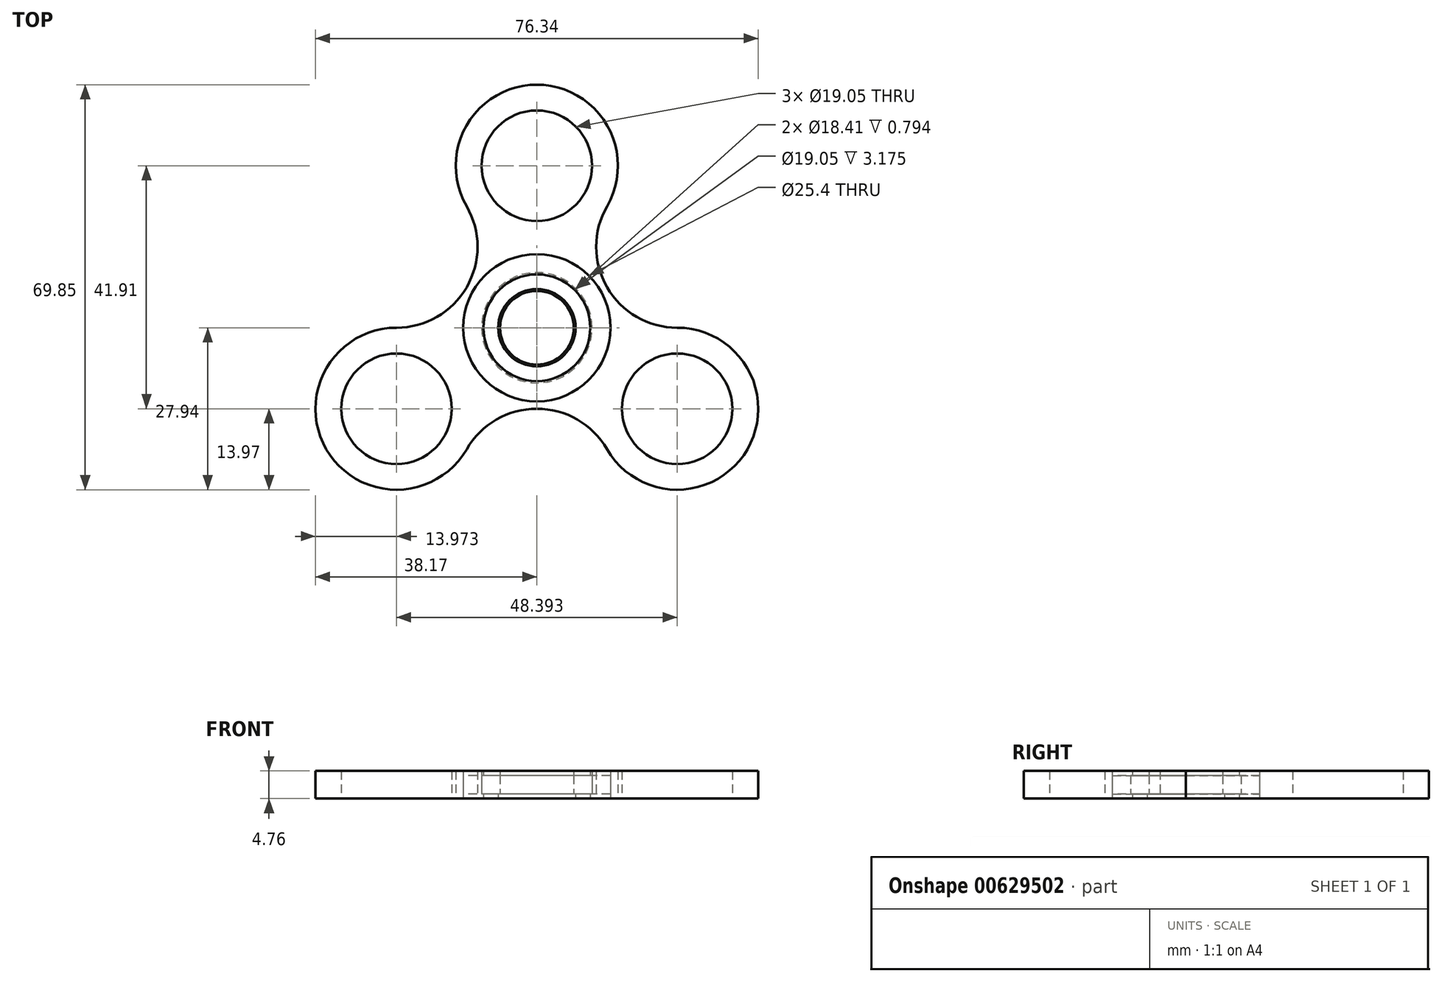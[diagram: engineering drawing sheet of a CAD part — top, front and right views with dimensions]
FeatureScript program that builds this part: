
annotation { "Feature Type Name" : "Feature", "Feature Type Description" : "" }
export const myFeature = defineFeature(function(context is Context, id is Id, definition is map)
    precondition{}
    {
        {
            var Q0;
            Q0=qCreatedBy(makeId("Top.planeOp"),FACE);
            var sketch = newSketch(context, id + "F0", { "sketchPlane" : qUnion([Q0])});
            skCircle(sketch, "E0", {"center": v(0, 0) * mm, "radius": 12.7 * mm});
            skCircle(sketch, "E1", {"center": v(0, 0) * mm, "radius": 9.2 * mm});
            skCircle(sketch, "E2", {"center": v(0, 0) * mm, "radius": 6.67 * mm});
            skSolve(sketch);
        }
        {
            var Q0;
            Q0=makeQuery(id+"F0.imprint","IMPRINT",FACE,{"disambiguationData":[TD([[makeQuery(id+"F0.imprint","IMPRINT",EDGE,{"derivedFrom":sQuery(id+"F0.wireOp",EDGE,"E0")}),1.0]])]});
            var Q1;
            Q1=makeQuery(id+"F0.imprint","IMPRINT",FACE,{"disambiguationData":[TD([[makeQuery(id+"F0.imprint","IMPRINT",EDGE,{"derivedFrom":sQuery(id+"F0.wireOp",EDGE,"E2")}),1.0]])]});
            extrude(context, id + "F1", {"entities" : qUnion([Q0, Q1]), "depth" : 0.8 * mm, "offsetDistance" : 25.4 * mm});
        }
        {
            var Q0;
            Q0=makeQuery(id+"F1.opExtrude","CAP_FACE",FACE,{"disambiguationData":[OSD([sQuery(id+"F0.wireOp",EDGE,"E2")])],"isStart":false});
            var sketch = newSketch(context, id + "F2", { "sketchPlane" : qUnion([Q0])});
            skCircle(sketch, "E3", {"center": v(0, 0) * mm, "radius": 12.7 * mm});
            skCircle(sketch, "E4", {"center": v(0, 0) * mm, "radius": 9.53 * mm});
            skCircle(sketch, "E5", {"center": v(0, 0) * mm, "radius": 6.35 * mm});
            skSolve(sketch);
        }
        {
            var Q0;
            Q0=makeQuery(id+"F2.imprint","IMPRINT",FACE,{"disambiguationData":[TD([[makeQuery(id+"F2.imprint","IMPRINT",EDGE,{"derivedFrom":sQuery(id+"F2.wireOp",EDGE,"E5")}),1.0]])]});
            var Q1;
            Q1=makeQuery(id+"F2.imprint","IMPRINT",FACE,{"disambiguationData":[TD([[makeQuery(id+"F2.imprint","IMPRINT",EDGE,{"derivedFrom":sQuery(id+"F2.wireOp",EDGE,"E3")}),1.0]])]});
            extrude(context, id + "F3", {"entities" : qUnion([Q0, Q1]), "depth" : 3.17 * mm, "offsetDistance" : 25.4 * mm});
        }
        {
            var Q0;
            Q0=makeQuery(id+"F3.opExtrude","CAP_FACE",FACE,{"disambiguationData":[OSD([sQuery(id+"F2.wireOp",EDGE,"E5")])],"isStart":false});
            var sketch = newSketch(context, id + "F4", { "sketchPlane" : qUnion([Q0])});
            skCircle(sketch, "E6", {"center": v(0, 0) * mm, "radius": 12.7 * mm});
            skCircle(sketch, "E7", {"center": v(0, 0) * mm, "radius": 9.2 * mm});
            skCircle(sketch, "E8", {"center": v(0, 0) * mm, "radius": 6.67 * mm});
            skSolve(sketch);
        }
        {
            var Q0;
            Q0=makeQuery(id+"F4.imprint","IMPRINT",FACE,{"disambiguationData":[TD([[makeQuery(id+"F4.imprint","IMPRINT",EDGE,{"derivedFrom":makeQuery(id+"F3.opExtrude","CAP_EDGE",EDGE,{"disambiguationData":[OSD([sQuery(id+"F2.wireOp",EDGE,"E5")])],"isStart":false})}),1.0]])]});
            var Q1;
            Q1=makeQuery(id+"F4.imprint","IMPRINT",FACE,{"disambiguationData":[TD([[makeQuery(id+"F4.imprint","IMPRINT",EDGE,{"derivedFrom":sQuery(id+"F4.wireOp",EDGE,"E6")}),1.0]])]});
            extrude(context, id + "F5", {"entities" : qUnion([Q0, Q1]), "depth" : 0.8 * mm, "offsetDistance" : 25.4 * mm});
        }
        {
            var Q0;
            Q0=qCreatedBy(makeId("Top.planeOp"),FACE);
            var sketch = newSketch(context, id + "F6", { "sketchPlane" : qUnion([Q0])});
            skCircle(sketch, "E9", {"center": v(0, 0) * mm, "radius": 12.7 * mm});
            skCircle(sketch, "E10", {"center": v(0, 0) * mm, "radius": 13.97 * mm});
            skArc(sketch, "E11", {"start": v(12.1, 20.96) * mm, "mid": v(0, 41.91) * mm, "end": v(-12.1, 20.96) * mm});
            skArc(sketch, "E12", {"start": v(-24.2, 0) * mm, "mid": v(-12.1, 6.99) * mm, "end": v(-12.1, 20.96) * mm});
            skArc(sketch, "E13", {"start": v(-24.2, 0) * mm, "mid": v(-36.3, -20.96) * mm, "end": v(-12.1, -20.96) * mm});
            skArc(sketch, "E14", {"start": v(12.1, -20.96) * mm, "mid": v(0, -13.97) * mm, "end": v(-12.1, -20.96) * mm});
            skArc(sketch, "E15", {"start": v(12.1, -20.95) * mm, "mid": v(36.3, -20.96) * mm, "end": v(24.2, 0) * mm});
            skArc(sketch, "E16", {"start": v(12.1, 20.95) * mm, "mid": v(12.1, 6.98) * mm, "end": v(24.2, 0) * mm});
            skCircle(sketch, "E17", {"center": v(0, 27.94) * mm, "radius": 9.53 * mm});
            skCircle(sketch, "E18", {"center": v(-24.2, -13.97) * mm, "radius": 9.53 * mm});
            skCircle(sketch, "E19", {"center": v(24.2, -13.97) * mm, "radius": 9.53 * mm});
            skSolve(sketch);
        }
        {
            var Q0;
            {var subQ5=sQuery(id+"F6.wireOp",EDGE,"E11");Q0=makeQuery(id+"F6.imprint","IMPRINT",FACE,{"disambiguationData":[TD([[makeQuery(id+"F6.imprint","IMPRINT",EDGE,{"derivedFrom":subQ5}),1.0]])]});}
            var Q1;
            {var subQ5=sQuery(id+"F6.wireOp",EDGE,"E13");Q1=makeQuery(id+"F6.imprint","IMPRINT",FACE,{"disambiguationData":[TD([[makeQuery(id+"F6.imprint","IMPRINT",EDGE,{"derivedFrom":subQ5}),1.0]])]});}
            var Q2;
            {var subQ5=sQuery(id+"F6.wireOp",EDGE,"E15");Q2=makeQuery(id+"F6.imprint","IMPRINT",FACE,{"disambiguationData":[TD([[makeQuery(id+"F6.imprint","IMPRINT",EDGE,{"derivedFrom":subQ5}),1.0]])]});}
            var Q3;
            Q3=makeQuery(id+"F6.imprint","IMPRINT",FACE,{"disambiguationData":[TD([[makeQuery(id+"F6.imprint","IMPRINT",EDGE,{"derivedFrom":sQuery(id+"F6.wireOp",EDGE,"E9")}),-1.0]])]});
            extrude(context, id + "F7", {"entities" : qUnion([Q0, Q1, Q2, Q3]), "depth" : 4.76 * mm, "offsetDistance" : 25.4 * mm});
        }
    });
